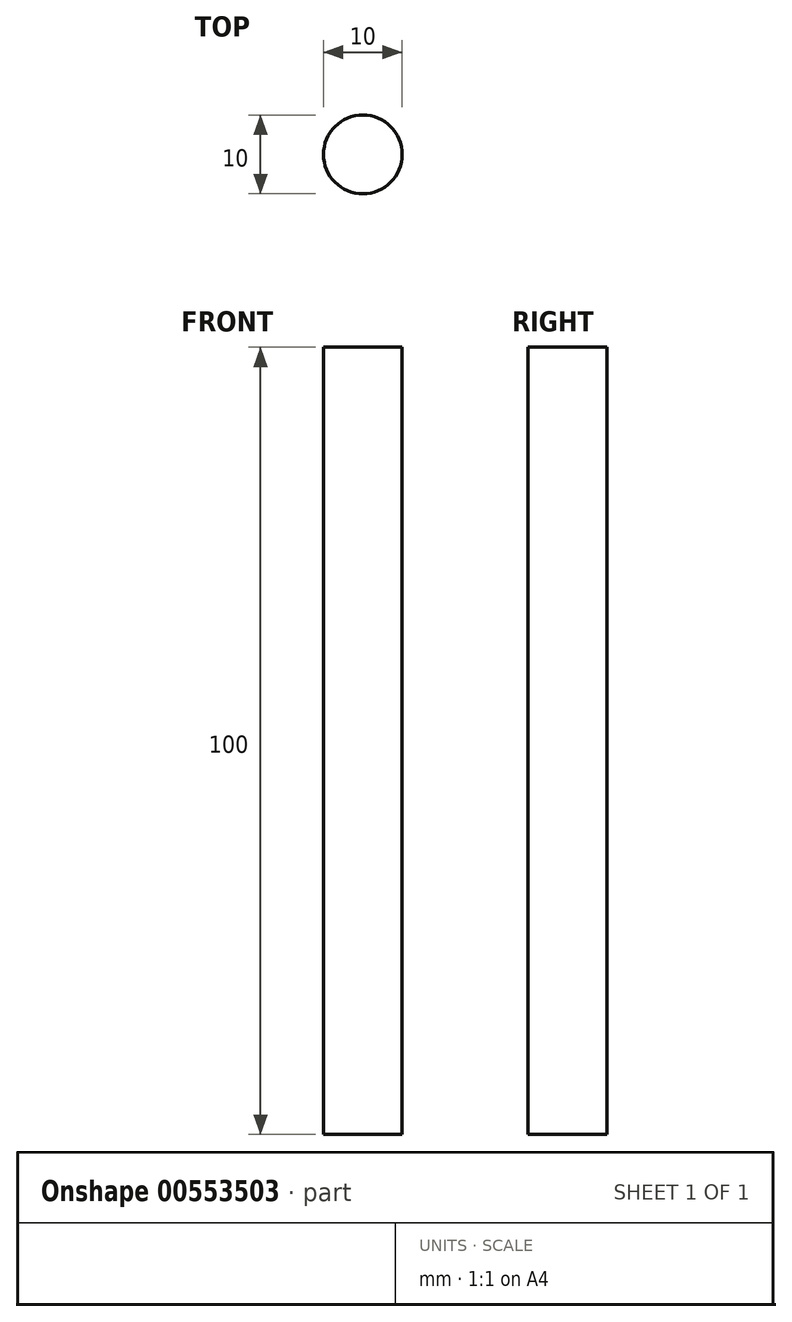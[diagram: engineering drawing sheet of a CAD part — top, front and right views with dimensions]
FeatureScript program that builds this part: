
annotation { "Feature Type Name" : "Feature", "Feature Type Description" : "" }
export const myFeature = defineFeature(function(context is Context, id is Id, definition is map)
    precondition{}
    {
        {
            var Q0;
            Q0=qCreatedBy(makeId("Top.planeOp"),FACE);
            var sketch = newSketch(context, id + "F0", { "sketchPlane" : qUnion([Q0])});
            skCircle(sketch, "E0", {"center": v(0, 0) * mm, "radius": 5 * mm});
            skSolve(sketch);
        }
        {
            var Q0;
            Q0 = qSketchRegion(id + "F0", true);
            extrude(context, id + "F1", {"entities" : qUnion([Q0]), "depth" : 100 * mm, "offsetDistance" : 25 * mm});
        }
    });
